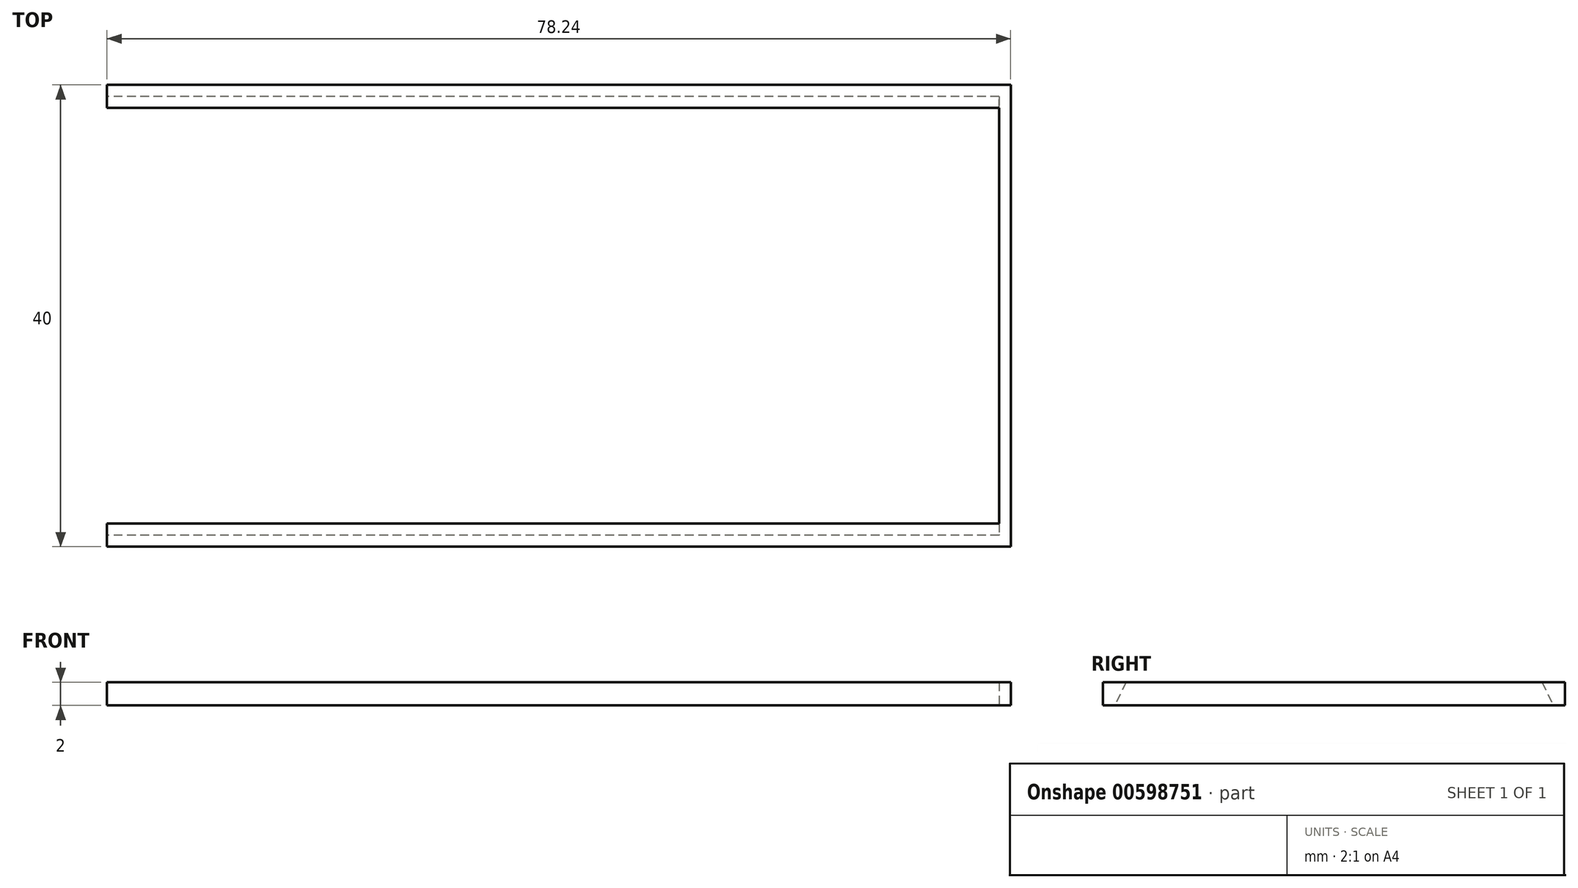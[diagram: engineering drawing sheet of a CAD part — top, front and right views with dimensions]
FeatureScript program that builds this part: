
annotation { "Feature Type Name" : "Feature", "Feature Type Description" : "" }
export const myFeature = defineFeature(function(context is Context, id is Id, definition is map)
    precondition{}
    {
        {
            var Q0;
            Q0=qCreatedBy(makeId("Top.planeOp"),FACE);
            var sketch = newSketch(context, id + "F0", { "sketchPlane" : qUnion([Q0])});
            skLineSegment(sketch, "E0.bottom", {"start": v(-39.12, 20) * mm, "end": v(39.13, 20) * mm});
            skLineSegment(sketch, "E0.top", {"start": v(-39.13, -20) * mm, "end": v(39.12, -20) * mm});
            skLineSegment(sketch, "E0.left", {"start": v(-39.12, 20) * mm, "end": v(-39.13, -20) * mm});
            skLineSegment(sketch, "E0.right", {"start": v(39.13, 20) * mm, "end": v(39.12, -20) * mm});
            skPoint(sketch, "E0.middle", {"position": v(0, 0) * mm});
            skSolve(sketch);
        }
        {
            var Q0;
            Q0=makeQuery(id+"F0.imprint","IMPRINT",FACE,{"disambiguationData":[TD([[makeQuery(id+"F0.imprint","IMPRINT",EDGE,{"derivedFrom":sQuery(id+"F0.wireOp",EDGE,"E0.bottom")}),-1.0]])]});
            extrude(context, id + "F1", {"entities" : qUnion([Q0]), "depth" : 2 * mm, "offsetDistance" : 25.4 * mm});
        }
        {
            var Q0;
            Q0=makeQuery(id+"F1.opExtrude","SWEPT_FACE",FACE,{"disambiguationData":[OSD([sQuery(id+"F0.wireOp",EDGE,"E0.left")])]});
            var sketch = newSketch(context, id + "F2", { "sketchPlane" : qUnion([Q0])});
            skLineSegment(sketch, "E1", {"start": v(-20, 2) * mm, "end": v(-18, 2) * mm});
            skLineSegment(sketch, "E2", {"start": v(-20, 0) * mm, "end": v(-19, 0) * mm});
            skLineSegment(sketch, "E3", {"start": v(-18, 2) * mm, "end": v(-19, 0) * mm});
            skLineSegment(sketch, "E4", {"start": v(20, 2) * mm, "end": v(18, 2) * mm});
            skLineSegment(sketch, "E5", {"start": v(20, 0) * mm, "end": v(19, 0) * mm});
            skLineSegment(sketch, "E6", {"start": v(18, 2) * mm, "end": v(19, 0) * mm});
            skSolve(sketch);
        }
        {
            var Q0;
            {var subQ0=sQuery(id+"F2.wireOp",EDGE,"E3");Q0=makeQuery(id+"F2.imprint","IMPRINT",FACE,{"disambiguationData":[TD([[makeQuery(id+"F2.imprint","IMPRINT",EDGE,{"derivedFrom":subQ0}),1.0]])]});}
            extrude(context, id + "F3", {"entities" : qUnion([Q0]), "operationType" : NewBodyOperationType.REMOVE, "oppositeDirection" : true, "depth" : 77.25 * mm, "offsetDistance" : 25.4 * mm});
        }
    });
